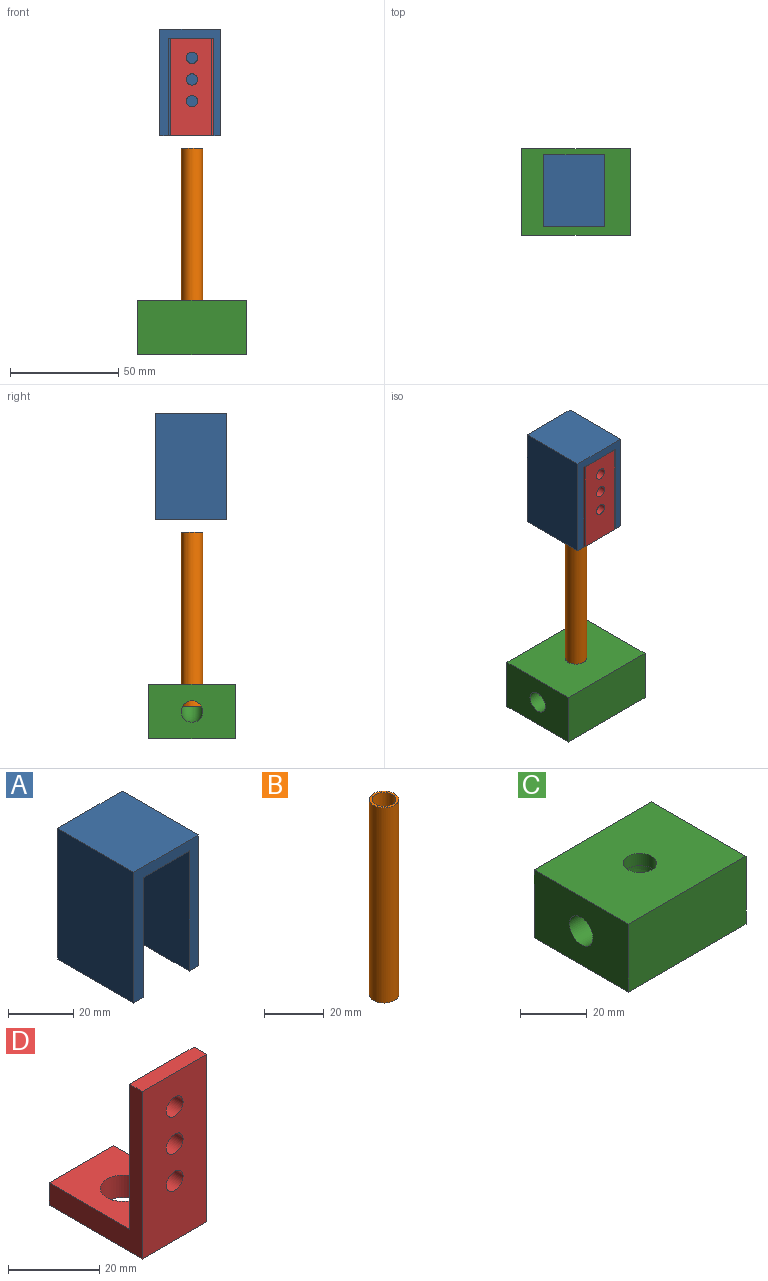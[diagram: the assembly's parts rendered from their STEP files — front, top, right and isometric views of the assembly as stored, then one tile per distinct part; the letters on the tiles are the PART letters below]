
ASSEMBLY  parts=4 mates=3
PART A: 10 faces, bbox 28x33x49 mm
  f0: plane 33x28mm, normal (0,0,-1), area 344mm2, adj f1,f2,f5,f6,f7,f8,f9
  f1: plane 45x20mm, normal (0,-1,0), area 900mm2, adj f0,f3,f7,f8
  f2: plane 49x28mm, normal (0,1,0), area 1372mm2, adj f0,f4,f6,f9
  f3: plane 29x20mm, normal (0,0,-1), area 580mm2, adj f1,f5,f7,f8
  f4: plane 33x28mm, normal (0,0,1), area 924mm2, adj f2,f5,f6,f9
  f5: plane 49x28mm, normal (0,-1,0), area 472mm2, adj f0,f3,f4,f6,f7,f8,f9
  f6: plane 49x33mm, normal (-1,0,0), area 1617mm2, adj f0,f2,f4,f5
  f7: plane 45x29mm, normal (1,0,0), area 1305mm2, adj f0,f1,f3,f5
  f8: plane 45x29mm, normal (-1,0,0), area 1305mm2, adj f0,f1,f3,f5
  f9: plane 49x33mm, normal (1,0,0), area 1617mm2, adj f0,f2,f4,f5
PART B: 4 faces, bbox 9.8x9.8x80 mm
  f0: cylinder r=4mm len=80mm, axis (0,0,-1), area 2010.6mm2, adj f2,f3
  f1: cylinder r=4.9mm len=80mm, axis (0,0,-1), area 2463mm2, adj f2,f3
  f2: plane 9.8x9.8mm, normal (0,0,1), area 25.2mm2, adj f0,f1
  f3: plane 9.8x9.8mm, normal (0,0,-1), area 25.2mm2, adj f0,f1
PART C: 9 faces, bbox 50x40x25 mm
  f0: plane 50x25mm, normal (0,1,0), area 1250mm2, adj f1,f3,f4,f5
  f1: plane 40x25mm, normal (-1,0,0), area 921.5mm2, adj f0,f2,f4,f5,f6
  f2: plane 50x25mm, normal (0,-1,0), area 1250mm2, adj f1,f3,f4,f5
  f3: plane 40x25mm, normal (1,0,0), area 1000mm2, adj f0,f2,f4,f5
  f4: plane 50x40mm, normal (0,0,1), area 1921.5mm2, adj f0,f1,f2,f3,f7
  f5: plane 50x40mm, normal (0,0,-1), area 2000mm2, adj f0,f1,f2,f3
  f6: cylinder r=5mm len=17mm, axis (-1,0,0), area 534.1mm2, adj f1,f8
  f7: cylinder r=5mm len=10mm, axis (0,0,-1), area 141.4mm2, adj f4,f8
  f8: torus R=8mm, axis (0,1,0), area 394.8mm2, adj f6,f7
PART D: 12 faces, bbox 20x29x45 mm
  f0: plane 39x20mm, normal (0,1,0), area 716.3mm2, adj f1,f3,f4,f6,f7,f8,f9
  f1: plane 45x29mm, normal (-1,0,0), area 330mm2, adj f0,f2,f4,f5,f9,f10
  f2: plane 29x20mm, normal (0,0,-1), area 501.5mm2, adj f1,f3,f5,f10,f11
  f3: plane 45x29mm, normal (1,0,0), area 330mm2, adj f0,f2,f4,f5,f9,f10
  f4: plane 20x4mm, normal (0,0,1), area 80mm2, adj f0,f1,f3,f5
  f5: plane 45x20mm, normal (0,-1,0), area 836.3mm2, adj f1,f2,f3,f4,f6,f7,f8
  f6: cylinder r=2.6mm len=5.2mm, axis (0,-1,0), area 65.3mm2, adj f0,f5
  f7: cylinder r=2.6mm len=5.2mm, axis (0,-1,0), area 65.3mm2, adj f0,f5
  f8: cylinder r=2.6mm len=5.2mm, axis (0,-1,0), area 65.3mm2, adj f0,f5
  f9: plane 25x20mm, normal (0,0,1), area 421.5mm2, adj f0,f1,f3,f10,f11
  f10: plane 20x6mm, normal (0,1,0), area 120mm2, adj f1,f2,f3,f9
  f11: cylinder r=5mm len=10mm, axis (0,0,1), area 188.5mm2, adj f2,f9
PLACE A t=(-31.13,11.96,44.01)mm
PLACE B t=(-30.26,-5.04,-41.89)mm
PLACE C t=(-30.26,-5.04,-44.4)mm
PLACE D t=(-30.26,-17.04,43.95)mm
MATE slider D.f11 <-> B.f0  axis (0,0,-1) through (-30.26,-5.04,43.95)mm
MATE planar A.f1 <-> D.f10  axis (0,-1,0) through (-31.13,7.96,44.01)mm
MATE slider C.f7 <-> B.f1  axis (0,0,1) through (-30.26,-5.04,-36.4)mm
